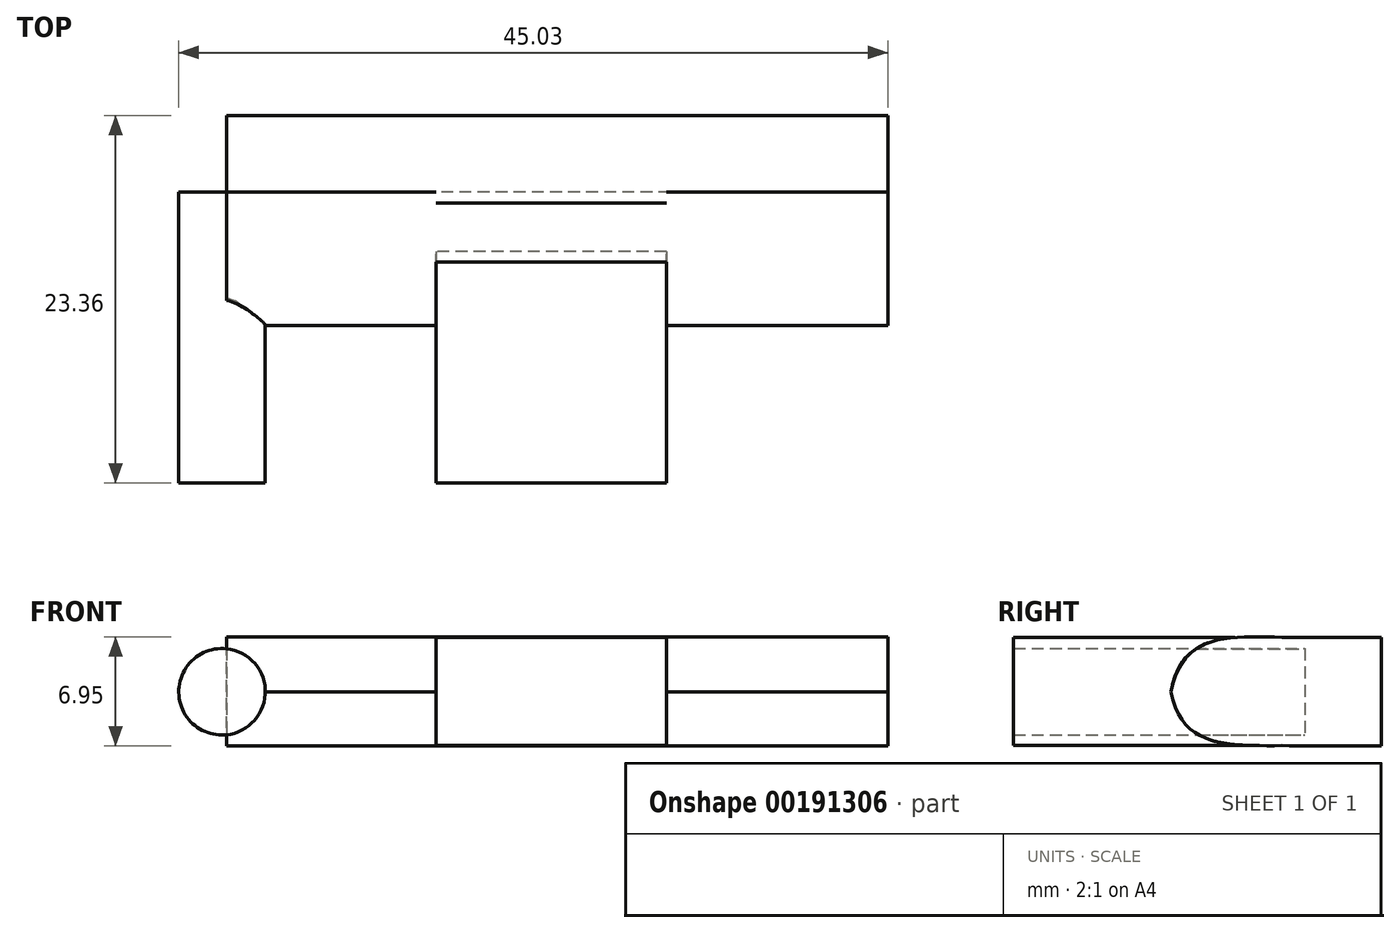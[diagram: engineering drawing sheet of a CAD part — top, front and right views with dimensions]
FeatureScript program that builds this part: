
annotation { "Feature Type Name" : "Feature", "Feature Type Description" : "" }
export const myFeature = defineFeature(function(context is Context, id is Id, definition is map)
    precondition{}
    {
        {
            var Q0;
            Q0=qCreatedBy(makeId("Right.planeOp"),FACE);
            var sketch = newSketch(context, id + "F0", { "sketchPlane" : qUnion([Q0])});
            skLineSegment(sketch, "E0", {"start": v(0, 3.45) * mm, "end": v(-4.88, 3.45) * mm});
            skLineSegment(sketch, "E1", {"start": v(-4.88, 3.45) * mm, "end": v(-4.88, 0) * mm});
            skLineSegment(sketch, "E2", {"start": v(-4.88, 0) * mm, "end": v(0, 0) * mm});
            skLineSegment(sketch, "E3", {"start": v(0, 0) * mm, "end": v(0, 3.45) * mm});
            skPoint(sketch, "E4", {"position": v(-13.36, 0) * mm});
            skFitSpline(sketch, "E5", {"points": [v(-4.88, 3.45) * mm, v(-13.36, 0) * mm], "startDerivative": vector(-11, -0.16) * mm, "endDerivative": vector(-2.22, -12.96) * mm});
            skPoint(sketch, "E6", {"position": v(-4.88, -3.45) * mm});
            skLineSegment(sketch, "E7", {"start": v(-4.88, 0) * mm, "end": v(-4.88, -3.45) * mm});
            skLineSegment(sketch, "E8", {"start": v(-4.88, -3.45) * mm, "end": v(0, -3.45) * mm});
            skLineSegment(sketch, "E9", {"start": v(0, -3.45) * mm, "end": v(0, 0) * mm});
            skFitSpline(sketch, "E10", {"points": [v(-4.88, -3.45) * mm, v(-13.36, 0) * mm], "startDerivative": vector(-11, 0.55) * mm, "endDerivative": vector(-2.22, 12.57) * mm});
            skSolve(sketch);
        }
        {
            var Q0;
            Q0 = qSketchRegion(id + "F0", true);
            extrude(context, id + "F1", {"entities" : qUnion([Q0]), "depth" : 42 * mm});
        }
        {
            var Q0;
            Q0=qCreatedBy(makeId("Front.planeOp"),FACE);
            cPlane(context, id + "F2", {"entities" : qUnion([Q0]), "cplaneType" : CPlaneType.OFFSET, "offset" : 4.88 * mm, "width" : 152.4 * mm, "height" : 152.4 * mm});
        }
        {
            var Q0;
            Q0=qCreatedBy(id+"F2.planeOp",FACE);
            var sketch = newSketch(context, id + "F3", { "sketchPlane" : qUnion([Q0])});
            skLineSegment(sketch, "E11.bottom", {"start": v(13.3, 3.45) * mm, "end": v(27.95, 3.45) * mm});
            skLineSegment(sketch, "E11.top", {"start": v(13.3, -3.4) * mm, "end": v(27.95, -3.4) * mm});
            skLineSegment(sketch, "E11.left", {"start": v(13.3, 3.45) * mm, "end": v(13.3, -3.4) * mm});
            skLineSegment(sketch, "E11.right", {"start": v(27.95, 3.45) * mm, "end": v(27.95, -3.4) * mm});
            skLineSegment(sketch, "E12", {"start": v(0, 9.2) * mm, "end": v(13.3, 9.2) * mm});
            skLineSegment(sketch, "E13", {"start": v(0, 12.9) * mm, "end": v(-3.03, 12.9) * mm});
            skLineSegment(sketch, "E14", {"start": v(0, 7.5) * mm, "end": v(2.47, 7.5) * mm});
            skLineSegment(sketch, "E15", {"start": v(0, 0) * mm, "end": v(-0.28, 0) * mm});
            skCircle(sketch, "E16", {"center": v(-0.28, 0) * mm, "radius": 2.75 * mm});
            skSolve(sketch);
        }
        {
            var Q0;
            Q0 = qSketchRegion(id + "F3", true);
            extrude(context, id + "F4", {"entities" : qUnion([Q0]), "operationType" : NewBodyOperationType.ADD, "depth" : 18.48 * mm});
        }
    });
